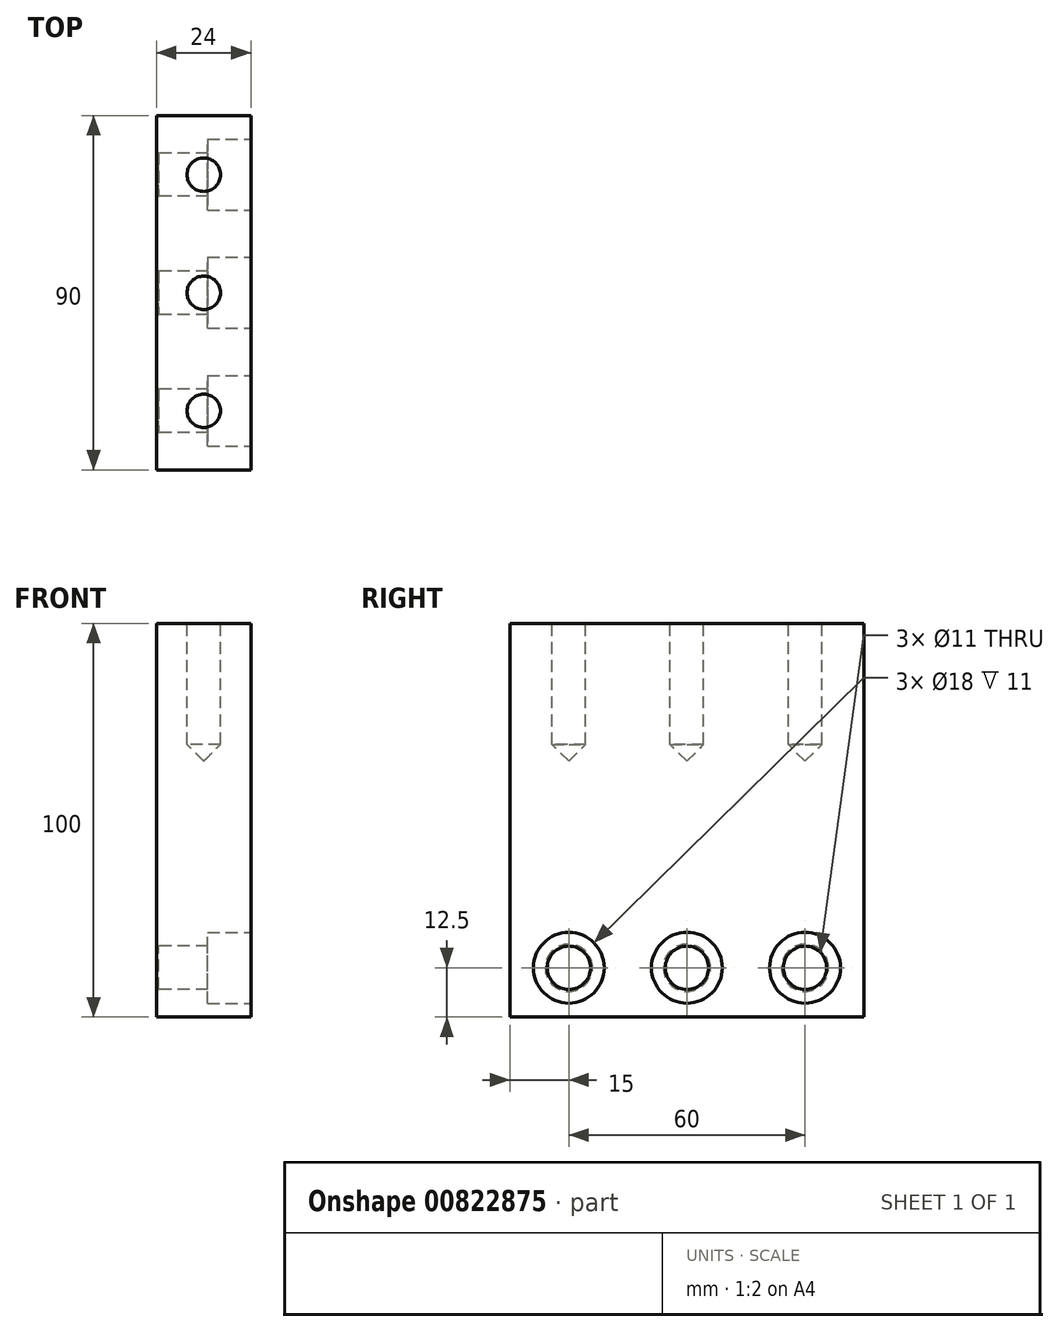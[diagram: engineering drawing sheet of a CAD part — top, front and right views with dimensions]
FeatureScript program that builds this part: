
annotation { "Feature Type Name" : "Feature", "Feature Type Description" : "" }
export const myFeature = defineFeature(function(context is Context, id is Id, definition is map)
    precondition{}
    {
        {
            var Q0;
            Q0=qCreatedBy(makeId("Right.planeOp"),FACE);
            var sketch = newSketch(context, id + "F0", { "sketchPlane" : qUnion([Q0])});
            skLineSegment(sketch, "E0.bottom", {"start": v(-45, -50) * mm, "end": v(45, -50) * mm});
            skLineSegment(sketch, "E0.top", {"start": v(-45, 50) * mm, "end": v(45, 50) * mm});
            skLineSegment(sketch, "E0.left", {"start": v(-45, -50) * mm, "end": v(-45, 50) * mm});
            skLineSegment(sketch, "E0.right", {"start": v(45, -50) * mm, "end": v(45, 50) * mm});
            skPoint(sketch, "E0.middle", {"position": v(0, 0) * mm});
            skLineSegment(sketch, "E1", {"start": v(-45, -25) * mm, "end": v(45, -25) * mm, "construction": true});
            skCircle(sketch, "E2", {"center": v(-30, -50) * mm, "radius": 9 * mm, "construction": true});
            skCircle(sketch, "E3.1.0.0", {"center": v(0, -50) * mm, "radius": 9 * mm, "construction": true});
            skCircle(sketch, "E3.2.0.0", {"center": v(30, -50) * mm, "radius": 9 * mm, "construction": true});
            skLineSegment(sketch, "E3.direction1", {"start": v(-30, -50) * mm, "end": v(0, -50) * mm, "construction": true});
            skLineSegment(sketch, "E4", {"start": v(-30, -50) * mm, "end": v(-30, -25) * mm, "construction": true});
            skLineSegment(sketch, "E5", {"start": v(-30, -37.5) * mm, "end": v(45, -37.5) * mm, "construction": true});
            skCircle(sketch, "E6", {"center": v(-30, -37.5) * mm, "radius": 5.5 * mm});
            skCircle(sketch, "E7.1.0.0", {"center": v(0, -37.5) * mm, "radius": 5.5 * mm});
            skCircle(sketch, "E7.2.0.0", {"center": v(30, -37.5) * mm, "radius": 5.5 * mm});
            skLineSegment(sketch, "E7.direction1", {"start": v(-30, -37.5) * mm, "end": v(0, -37.5) * mm, "construction": true});
            skSolve(sketch);
        }
        {
            var Q0;
            Q0 = qSketchRegion(id + "F0", true);
            extrude(context, id + "F1", {"entities" : qUnion([Q0]), "depth" : 24 * mm, "offsetDistance" : 25 * mm});
        }
        {
            var Q0;
            Q0=makeQuery(id+"F1.opExtrude","CAP_FACE",FACE,{"disambiguationData":[OSD([sQuery(id+"F0.wireOp",EDGE,"E0.bottom"),sQuery(id+"F0.wireOp",EDGE,"E0.top"),sQuery(id+"F0.wireOp",EDGE,"E0.left"),sQuery(id+"F0.wireOp",EDGE,"E0.right"),sQuery(id+"F0.wireOp",EDGE,"E6"),sQuery(id+"F0.wireOp",EDGE,"E7.1.0.0"),sQuery(id+"F0.wireOp",EDGE,"E7.2.0.0")])],"isStart":false});
            var sketch = newSketch(context, id + "F2", { "sketchPlane" : qUnion([Q0])});
            skCircle(sketch, "E8.0", {"center": v(-30, -37.5) * mm, "radius": 5.5 * mm, "construction": true});
            skCircle(sketch, "E9", {"center": v(-30, -37.5) * mm, "radius": 9 * mm});
            skCircle(sketch, "E10.1.0.0", {"center": v(0, -37.5) * mm, "radius": 9 * mm});
            skCircle(sketch, "E10.2.0.0", {"center": v(30, -37.5) * mm, "radius": 9 * mm});
            skLineSegment(sketch, "E10.direction1", {"start": v(-30, -37.5) * mm, "end": v(0, -37.5) * mm, "construction": true});
            skSolve(sketch);
        }
        {
            var Q0;
            Q0 = qSketchRegion(id + "F2", true);
            extrude(context, id + "F3", {"entities" : qUnion([Q0]), "operationType" : NewBodyOperationType.REMOVE, "oppositeDirection" : true, "depth" : 11 * mm, "offsetDistance" : 25 * mm});
        }
        {
            var Q0;
            Q0=makeQuery(id+"F1.opExtrude","SWEPT_FACE",FACE,{"disambiguationData":[OSD([sQuery(id+"F0.wireOp",EDGE,"E0.top")])]});
            var sketch = newSketch(context, id + "F4", { "sketchPlane" : qUnion([Q0])});
            skLineSegment(sketch, "E11.0.0", {"start": v(0, 45) * mm, "end": v(0, -45) * mm, "construction": true});
            skLineSegment(sketch, "E11.0.1", {"start": v(0, -45) * mm, "end": v(24, -45) * mm, "construction": true});
            skLineSegment(sketch, "E11.0.2", {"start": v(24, -45) * mm, "end": v(24, 45) * mm, "construction": true});
            skLineSegment(sketch, "E11.0.3", {"start": v(24, 45) * mm, "end": v(0, 45) * mm, "construction": true});
            skLineSegment(sketch, "E12", {"start": v(12, 45) * mm, "end": v(12, -30) * mm, "construction": true});
            skCircle(sketch, "E13", {"center": v(12, -30) * mm, "radius": 4.25 * mm});
            skCircle(sketch, "E14.0.1.0", {"center": v(12, 0) * mm, "radius": 4.25 * mm});
            skCircle(sketch, "E14.0.2.0", {"center": v(12, 30) * mm, "radius": 4.25 * mm});
            skLineSegment(sketch, "E14.direction1", {"start": v(12, -30) * mm, "end": v(37, -30) * mm, "construction": true});
            skLineSegment(sketch, "E14.direction2", {"start": v(12, -30) * mm, "end": v(12, 0) * mm, "construction": true});
            skSolve(sketch);
        }
        {
            var Q0;
            Q0 = qSketchRegion(id + "F4", true);
            extrude(context, id + "F5", {"entities" : qUnion([Q0]), "operationType" : NewBodyOperationType.REMOVE, "oppositeDirection" : true, "depth" : 35 * mm, "offsetDistance" : 25 * mm});
        }
        {
            var Q0;
            Q0=makeQuery(id+"F5.boolean.opBoolean","COPY",FACE,{"derivedFrom":makeQuery(id+"F5.opExtrude","CAP_FACE",FACE,{"disambiguationData":[OSD([sQuery(id+"F4.wireOp",EDGE,"E14.0.2.0")])],"isStart":false})});
            var Q1;
            Q1=makeQuery(id+"F5.boolean.opBoolean","COPY",FACE,{"derivedFrom":makeQuery(id+"F5.opExtrude","CAP_FACE",FACE,{"disambiguationData":[OSD([sQuery(id+"F4.wireOp",EDGE,"E14.0.1.0")])],"isStart":false})});
            var Q2;
            Q2=makeQuery(id+"F5.boolean.opBoolean","COPY",FACE,{"derivedFrom":makeQuery(id+"F5.opExtrude","CAP_FACE",FACE,{"disambiguationData":[OSD([sQuery(id+"F4.wireOp",EDGE,"E13")])],"isStart":false})});
            chamfer(context, id + "F6", {"entities" : qUnion([Q0, Q1, Q2]), "width" : 4.25 * mm, "tangentPropagation" : true});
        }
        {
            var Q0;
            Q0=makeQuery(id+"F1.opExtrude","CAP_EDGE",EDGE,{"disambiguationData":[OSD([sQuery(id+"F0.wireOp",EDGE,"E6")])],"isStart":true});
            var Q1;
            Q1=makeQuery(id+"F1.opExtrude","CAP_EDGE",EDGE,{"disambiguationData":[OSD([sQuery(id+"F0.wireOp",EDGE,"E7.1.0.0")])],"isStart":true});
            var Q2;
            Q2=makeQuery(id+"F1.opExtrude","CAP_EDGE",EDGE,{"disambiguationData":[OSD([sQuery(id+"F0.wireOp",EDGE,"E7.2.0.0")])],"isStart":true});
            var Q3;
            Q3=makeQuery(id+"F5.boolean.opBoolean","COPY",EDGE,{"derivedFrom":makeQuery(id+"F5.opExtrude","CAP_EDGE",EDGE,{"disambiguationData":[OSD([sQuery(id+"F4.wireOp",EDGE,"E14.0.2.0")])],"isStart":true})});
            var Q4;
            Q4=makeQuery(id+"F5.boolean.opBoolean","COPY",EDGE,{"derivedFrom":makeQuery(id+"F5.opExtrude","CAP_EDGE",EDGE,{"disambiguationData":[OSD([sQuery(id+"F4.wireOp",EDGE,"E14.0.1.0")])],"isStart":true})});
            var Q5;
            Q5=makeQuery(id+"F5.boolean.opBoolean","COPY",EDGE,{"derivedFrom":makeQuery(id+"F5.opExtrude","CAP_EDGE",EDGE,{"disambiguationData":[OSD([sQuery(id+"F4.wireOp",EDGE,"E13")])],"isStart":true})});
            var Q6;
            Q6=makeQuery(id+"F3.boolean.opBoolean","COPY",EDGE,{"derivedFrom":makeQuery(id+"F3.opExtrude","CAP_EDGE",EDGE,{"disambiguationData":[OSD([sQuery(id+"F2.wireOp",EDGE,"E9")])],"isStart":true})});
            var Q7;
            Q7=makeQuery(id+"F3.boolean.opBoolean","COPY",EDGE,{"derivedFrom":makeQuery(id+"F3.opExtrude","CAP_EDGE",EDGE,{"disambiguationData":[OSD([sQuery(id+"F2.wireOp",EDGE,"E10.1.0.0")])],"isStart":true})});
            var Q8;
            Q8=makeQuery(id+"F3.boolean.opBoolean","COPY",EDGE,{"derivedFrom":makeQuery(id+"F3.opExtrude","CAP_EDGE",EDGE,{"disambiguationData":[OSD([sQuery(id+"F2.wireOp",EDGE,"E10.2.0.0")])],"isStart":true})});
            chamfer(context, id + "F7", {"entities" : qUnion([Q0, Q1, Q2, Q3, Q4, Q5, Q6, Q7, Q8]), "width" : 0.5 * mm, "tangentPropagation" : true});
        }
    });
